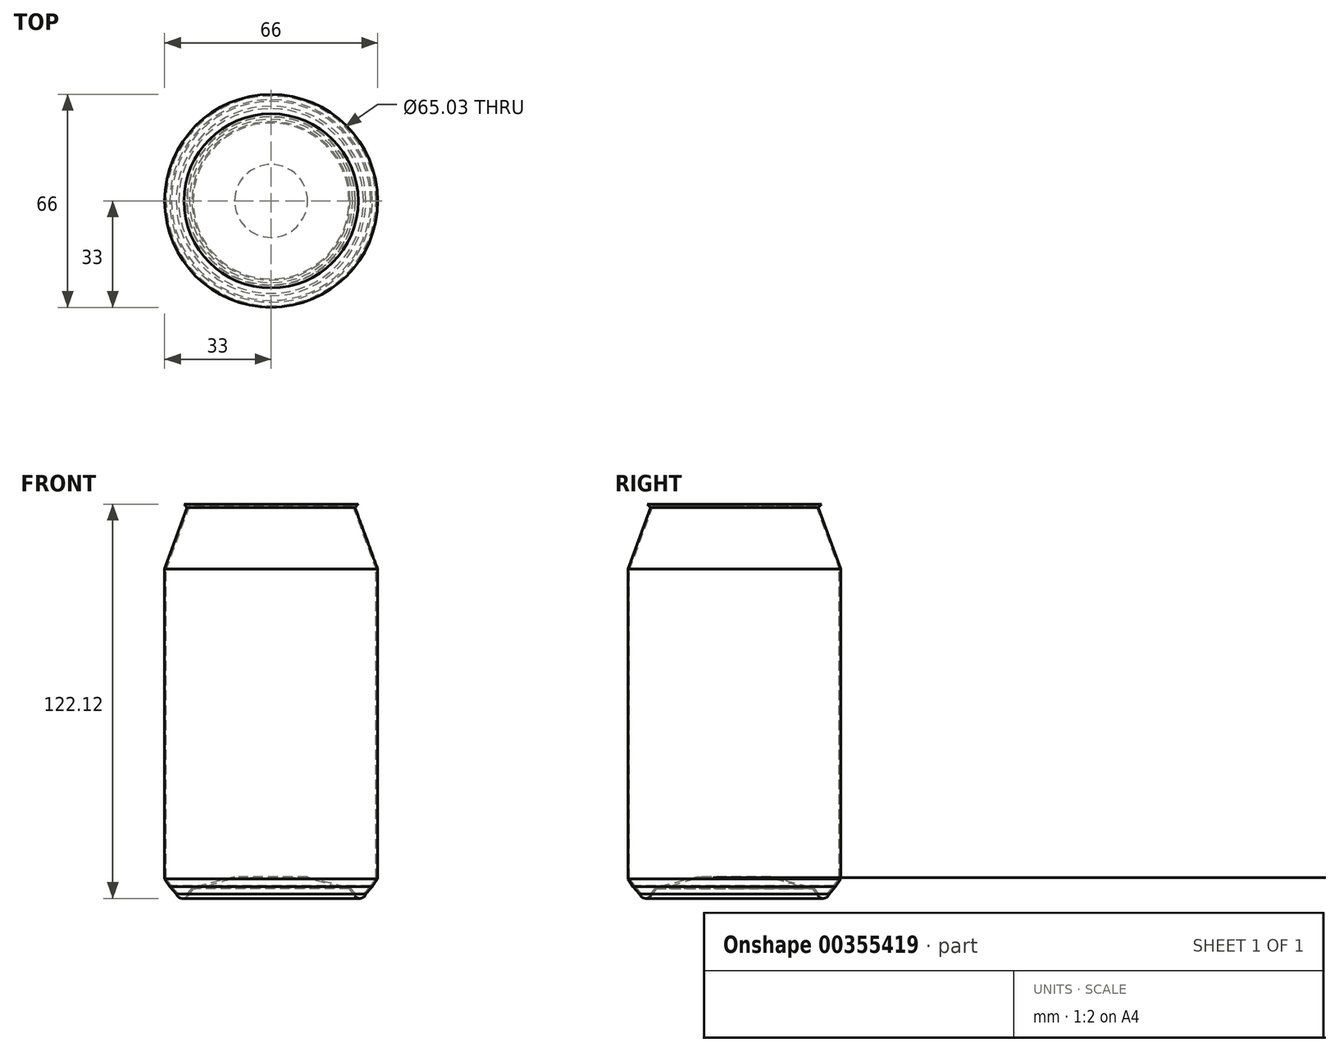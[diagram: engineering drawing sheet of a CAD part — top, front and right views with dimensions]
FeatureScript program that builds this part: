
annotation { "Feature Type Name" : "Feature", "Feature Type Description" : "" }
export const myFeature = defineFeature(function(context is Context, id is Id, definition is map)
    precondition{}
    {
        {
            var Q0;
            Q0=qCreatedBy(makeId("Front.planeOp"),FACE);
            var sketch = newSketch(context, id + "F0", { "sketchPlane" : qUnion([Q0])});
            skLineSegment(sketch, "E0", {"start": v(33, -48.39) * mm, "end": v(33, 47.64) * mm});
            skLineSegment(sketch, "E1", {"start": v(33, 47.64) * mm, "end": v(26, 66.64) * mm});
            skLineSegment(sketch, "E2", {"start": v(26, 66.64) * mm, "end": v(27, 67.64) * mm});
            skLineSegment(sketch, "E3", {"start": v(27, 67.64) * mm, "end": v(0, 67.64) * mm});
            skLineSegment(sketch, "E4", {"start": v(33, -48.39) * mm, "end": v(31.37, -50.78) * mm});
            skLineSegment(sketch, "E5", {"start": v(31.37, -50.78) * mm, "end": v(29.38, -53.12) * mm});
            skLineSegment(sketch, "E6", {"start": v(29.38, -53.12) * mm, "end": v(29.32, -53.27) * mm});
            skLineSegment(sketch, "E7", {"start": v(25.9, -53.73) * mm, "end": v(24.17, -51.53) * mm});
            skLineSegment(sketch, "E8", {"start": v(0, 104.7) * mm, "end": v(0, -129.63) * mm, "construction": true});
            skFitSpline(sketch, "E9", {"points": [v(0, -48.36) * mm, v(11.01, -48.28) * mm, v(24.17, -51.53) * mm], "startDerivative": vector(8.05, 0.54) * mm, "endDerivative": vector(23, -1.77) * mm});
            skPoint(sketch, "E10.visualSharp", {"position": v(28, -56.36) * mm});
            skArc(sketch, "E10.filletArc", {"start": v(25.9, -53.73) * mm, "mid": v(27.74, -54.47) * mm, "end": v(29.32, -53.27) * mm});
            skLineSegment(sketch, "E11", {"start": v(0, 67.64) * mm, "end": v(0, 67.14) * mm});
            skLineSegment(sketch, "E12", {"start": v(0, 67.14) * mm, "end": v(25.28, 67.14) * mm});
            skLineSegment(sketch, "E13", {"start": v(25.28, 67.14) * mm, "end": v(32.51, 47.52) * mm});
            skLineSegment(sketch, "E14", {"start": v(32.51, 47.52) * mm, "end": v(32.51, -48.28) * mm});
            skLineSegment(sketch, "E15", {"start": v(32.51, -48.28) * mm, "end": v(30.85, -50.63) * mm});
            skLineSegment(sketch, "E16", {"start": v(30.85, -50.63) * mm, "end": v(28.63, -53.22) * mm});
            skLineSegment(sketch, "E17", {"start": v(28.63, -53.22) * mm, "end": v(26.15, -53.22) * mm});
            skLineSegment(sketch, "E18", {"start": v(26.15, -53.22) * mm, "end": v(24.56, -51.22) * mm});
            skLineSegment(sketch, "E19", {"start": v(24.56, -51.22) * mm, "end": v(11.3, -47.86) * mm});
            skLineSegment(sketch, "E20", {"start": v(11.3, -47.86) * mm, "end": v(0, -47.86) * mm});
            skLineSegment(sketch, "E21", {"start": v(0, -47.86) * mm, "end": v(0, -48.36) * mm});
            skSolve(sketch);
        }
        {
            var Q0;
            Q0=qSketchRegion(id+"F0",true);
            var Q1;
            Q1=sQuery(id+"F0.wireOp",EDGE,"E8");
            revolve(context, id + "F1", {"entities" : qUnion([Q0]), "axis" : qUnion([Q1]), "revolveType" : RevolveType.FULL});
        }
    });
